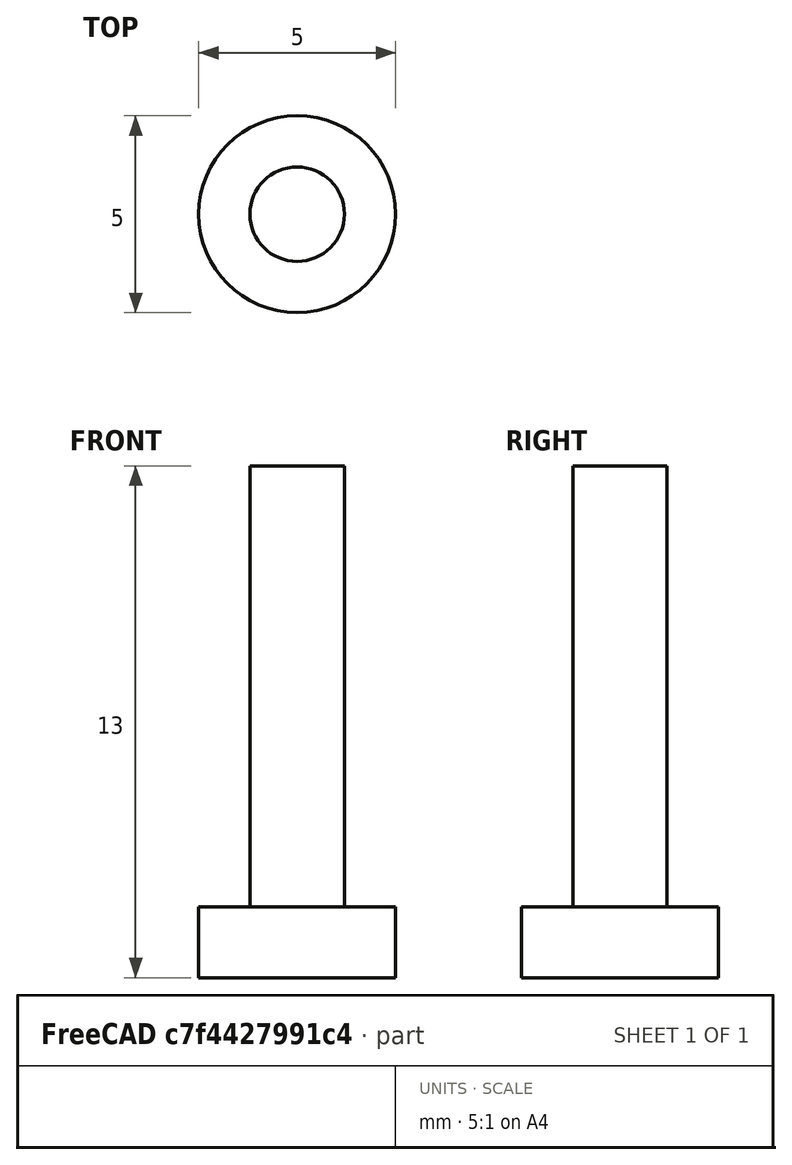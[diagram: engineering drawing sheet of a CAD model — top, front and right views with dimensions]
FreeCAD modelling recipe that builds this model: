
FCSTD DOCUMENT  (FreeCAD 0.16R6706 (Git))
Label: ButtonSmall
License: All rights reserved
LicenseURL: http://de.wikipedia.org/wiki/Alle_Rechte_vorbehalten
objects: Sketcher::SketchObject×1, PartDesign::Revolution×1
note: 3 computed .brp shape members not serialized (recipe doc carries the construction recipe); baked Part::Feature solids carry a one-line shape summary decoded from their .brp

FEATURE [Sketcher::SketchObject] Sketch
  Placement = pos=(0,0,0) rot=(1,0,0;1.5708rad)
  sketch-geometry (6):
    g0: LineSegment StartX=0 StartY=13 StartZ=0 EndX=1.2 EndY=13 EndZ=0
    g1: LineSegment StartX=1.2 StartY=13 StartZ=0 EndX=1.2 EndY=1.8 EndZ=0
    g2: LineSegment StartX=1.2 StartY=1.8 StartZ=0 EndX=2.5 EndY=1.8 EndZ=0
    g3: LineSegment StartX=2.5 StartY=1.8 StartZ=0 EndX=2.5 EndY=0 EndZ=0
    g4: LineSegment StartX=2.5 StartY=0 StartZ=0 EndX=0 EndY=0 EndZ=0
    g5: LineSegment StartX=0 StartY=0 StartZ=0 EndX=0 EndY=13 EndZ=0
  constraints (17):
    c: PointOnObject(g0,g-2)
    c: Horizontal(g0)
    c: Coincident(g0,g1)
    c: Vertical(g1)
    c: Coincident(g1,g2)
    c: Horizontal(g2)
    c: Coincident(g2,g3)
    c: PointOnObject(g3,g-1)
    c: Vertical(g3)
    c: Coincident(g3,g4)
    c: Coincident(g4,g-1)
    c: Coincident(g4,g5)
    c: Coincident(g5,g0)
    c: DistanceY(g-1,g0) = 13
    c: DistanceY(g3,g2) = 1.8
    c: DistanceX(g0,g0) = 1.2
    c: DistanceX(g-1,g3) = 2.5
FEATURE [PartDesign::Revolution] Revolution
  Angle = 360
  Axis = (0,0,1)
  Base = (0,0,0)
  Placement = pos=(0,0,0) rot=(1,0,0;1.5708rad)
  ReferenceAxis = -> Sketch [V_Axis]
  Reversed = true
  Sketch = -> Sketch
